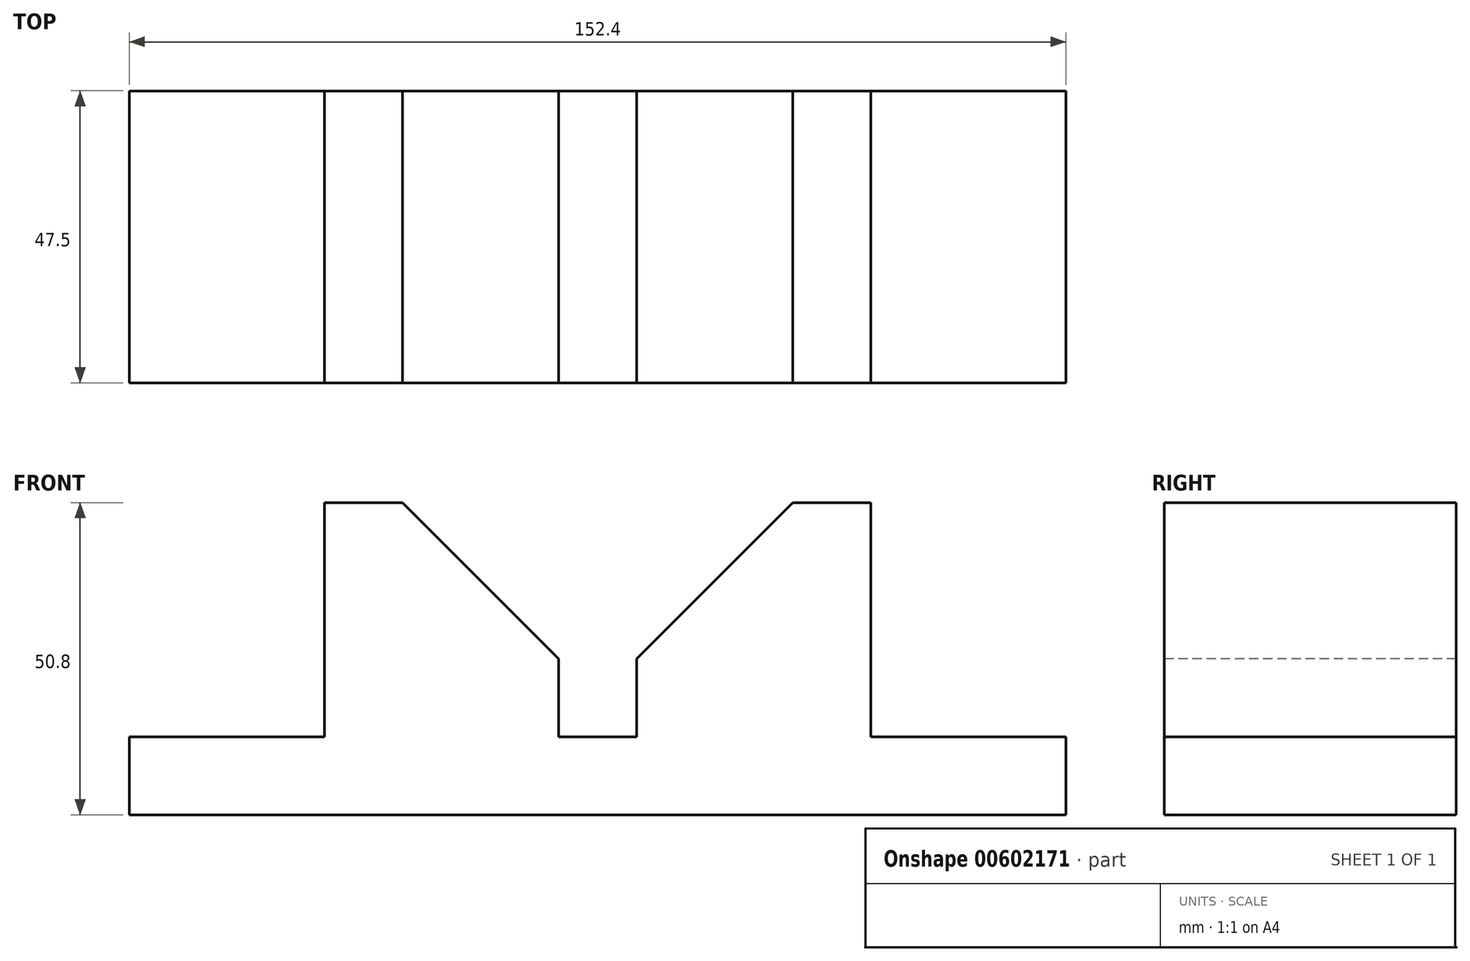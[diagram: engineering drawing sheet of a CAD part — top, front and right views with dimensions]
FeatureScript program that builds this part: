
annotation { "Feature Type Name" : "Feature", "Feature Type Description" : "" }
export const myFeature = defineFeature(function(context is Context, id is Id, definition is map)
    precondition{}
    {
        {
            var Q0;
            Q0=qCreatedBy(makeId("Front.planeOp"),FACE);
            var sketch = newSketch(context, id + "F0", { "sketchPlane" : qUnion([Q0])});
            skLineSegment(sketch, "E0.bottom", {"start": v(0, 0) * mm, "end": v(152.4, 0) * mm});
            skLineSegment(sketch, "E0.left", {"start": v(0, 0) * mm, "end": v(0, 12.7) * mm});
            skLineSegment(sketch, "E0.right", {"start": v(152.4, 0) * mm, "end": v(152.4, 12.7) * mm});
            skLineSegment(sketch, "E1", {"start": v(0, 0) * mm, "end": v(31.75, 0) * mm});
            skLineSegment(sketch, "E2", {"start": v(152.4, 0) * mm, "end": v(120.65, 0) * mm});
            skLineSegment(sketch, "E3", {"start": v(31.75, 12.7) * mm, "end": v(31.75, 50.8) * mm});
            skLineSegment(sketch, "E4", {"start": v(120.65, 12.7) * mm, "end": v(120.65, 50.8) * mm});
            skLineSegment(sketch, "E5", {"start": v(31.75, 50.8) * mm, "end": v(44.45, 50.8) * mm});
            skLineSegment(sketch, "E6", {"start": v(120.65, 50.8) * mm, "end": v(107.95, 50.8) * mm});
            skLineSegment(sketch, "E7", {"start": v(69.85, 12.7) * mm, "end": v(69.85, 25.4) * mm});
            skLineSegment(sketch, "E8", {"start": v(82.55, 12.7) * mm, "end": v(82.55, 25.4) * mm});
            skLineSegment(sketch, "E9", {"start": v(44.45, 50.8) * mm, "end": v(69.85, 25.4) * mm});
            skLineSegment(sketch, "E10", {"start": v(107.95, 50.8) * mm, "end": v(82.55, 25.4) * mm});
            skLineSegment(sketch, "E11", {"start": v(120.65, 12.7) * mm, "end": v(152.4, 12.7) * mm});
            skLineSegment(sketch, "E12", {"start": v(31.75, 12.7) * mm, "end": v(0, 12.7) * mm});
            skLineSegment(sketch, "E13", {"start": v(69.85, 12.7) * mm, "end": v(82.55, 12.7) * mm});
            skSolve(sketch);
        }
        {
            var Q0;
            Q0=makeQuery(id+"F0.imprint","IMPRINT",FACE,{"disambiguationData":[TD([[makeQuery(id+"F0.imprint","IMPRINT",EDGE,{"derivedFrom":sQuery(id+"F0.wireOp",EDGE,"E0.bottom")}),1.0]])]});
            extrude(context, id + "F1", {"entities" : qUnion([Q0]), "oppositeDirection" : true, "depth" : 47.5 * mm, "offsetDistance" : 25.4 * mm});
        }
    });
